# Revit family: Microwave tms
name_source: partatom
category: Specialty Equipment
revit_build: Autodesk Revit Architecture 2012 (Build: 20110916_2132(x64)
units: mm (PartAtom-declared; Revit-internal decimal feet)

## types (3) — shared parameters
Case = Metal - Firring
Glass = Glass - black
Key gaps = 0.2 cm
LED screen = Glass - black

## per-type parameters (varying)
| type | Depth | Front Panel | Height | Keypad Height | Keypad elevation | Knob elevation | Knob radius | Knob socket radius | Width |
| 60-W x 40-H x 30-D Aluminum | 31.6 cm | Metal - Aluminium | 38.2 cm | 10 cm | 13.49 cm | 9.25 cm | 3.25 cm | 3.45 cm | 59.5 cm |
| 60-W x 40-H x 30-D Black | 31.6 cm | Metal - Black Anodized Aluminum | 38.2 cm | 10 cm | 13.49 cm | 9.25 cm | 3.25 cm | 3.45 cm | 59.5 cm |
| 46.5-W x 28-H x 34-D Aluminum | 34 cm | Metal - Aluminium | 28 cm | 5.5 cm | 11.76 cm | 8.38 cm | 2.38 cm | 2.58 cm | 48.5 cm |

## geometry (parser evidence)
native form markers: Sweep x3
no freeform markers — native parametric forms only
